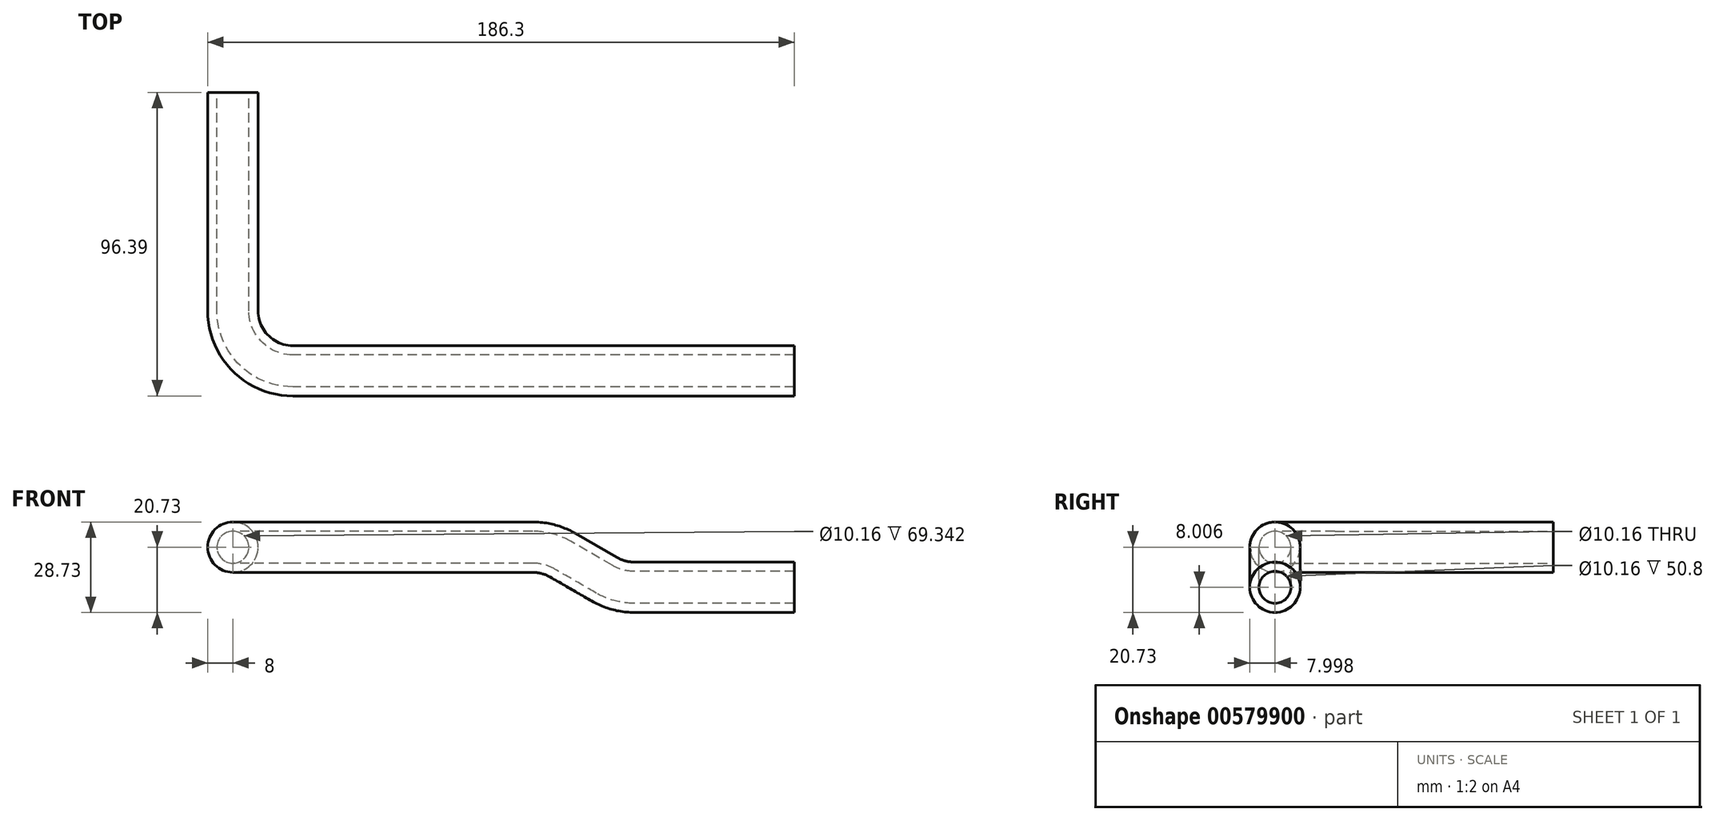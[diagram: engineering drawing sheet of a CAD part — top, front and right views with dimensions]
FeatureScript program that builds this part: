
annotation { "Feature Type Name" : "Feature", "Feature Type Description" : "" }
export const myFeature = defineFeature(function(context is Context, id is Id, definition is map)
    precondition{}
    {
        {
            var Q0;
            Q0=qCreatedBy(makeId("Front.planeOp"),FACE);
            var sketch = newSketch(context, id + "F0", { "sketchPlane" : qUnion([Q0])});
            skCircle(sketch, "E0", {"center": v(0, 0) * mm, "radius": 8 * mm});
            skCircle(sketch, "E1", {"center": v(0, 0) * mm, "radius": 5.08 * mm});
            skSolve(sketch);
        }
        {
            var Q0;
            Q0=qSketchRegion(id+"F0",true);
            extrude(context, id + "F1", {"entities" : qUnion([Q0]), "depth" : 69.34 * mm, "offsetDistance" : 25.4 * mm});
        }
        {
            var Q0;
            Q0=makeQuery(id+"F1.opExtrude","CAP_FACE",FACE,{"disambiguationData":[OSD([sQuery(id+"F0.wireOp",EDGE,"E0"),sQuery(id+"F0.wireOp",EDGE,"E1")])],"isStart":false});
            var sketch = newSketch(context, id + "F2", { "sketchPlane" : qUnion([Q0])});
            skCircle(sketch, "E2", {"center": v(0, 0) * mm, "radius": 5.08 * mm});
            skCircle(sketch, "E3", {"center": v(0, 0) * mm, "radius": 8 * mm});
            skLineSegment(sketch, "E4", {"start": v(19.05, 10.1) * mm, "end": v(19.05, -9.92) * mm});
            skSolve(sketch);
        }
        {
            var Q0;
            Q0 = qSketchRegion(id + "F2", true);
            var Q1;
            Q1=sQuery(id+"F2.wireOp",EDGE,"E4");
            revolve(context, id + "F3", {"operationType" : NewBodyOperationType.ADD, "entities" : qUnion([Q0]), "axis" : qUnion([Q1]), "revolveType" : RevolveType.ONE_DIRECTION, "oppositeDirection" : true, "angle" : 90 * degree});
        }
        {
            var Q0;
            Q0=makeQuery(id+"F3.opRevolve","CAP_FACE",FACE,{"disambiguationData":[OSD([sQuery(id+"F2.wireOp",EDGE,"E2"),sQuery(id+"F2.wireOp",EDGE,"E3")])],"isStart":false});
            var sketch = newSketch(context, id + "F4", { "sketchPlane" : qUnion([Q0])});
            skCircle(sketch, "E5", {"center": v(-88.4, 0) * mm, "radius": 8 * mm});
            skCircle(sketch, "E6", {"center": v(-88.4, 0) * mm, "radius": 5.08 * mm});
            skSolve(sketch);
        }
        {
            var Q0;
            Q0 = qSketchRegion(id + "F4", true);
            extrude(context, id + "F5", {"entities" : qUnion([Q0]), "operationType" : NewBodyOperationType.ADD, "depth" : 76.2 * mm, "offsetDistance" : 25.4 * mm});
        }
        {
            var Q0;
            Q0=makeQuery(id+"F5.opExtrude","CAP_FACE",FACE,{"disambiguationData":[OSD([sQuery(id+"F4.wireOp",EDGE,"E5"),sQuery(id+"F4.wireOp",EDGE,"E6")])],"isStart":false});
            var sketch = newSketch(context, id + "F6", { "sketchPlane" : qUnion([Q0])});
            skCircle(sketch, "E7", {"center": v(-88.4, 0) * mm, "radius": 8 * mm});
            skCircle(sketch, "E8", {"center": v(-88.4, 0) * mm, "radius": 5.08 * mm});
            skLineSegment(sketch, "E9", {"start": v(-98.35, -19.05) * mm, "end": v(-76.26, -19.05) * mm});
            skSolve(sketch);
        }
        {
            var Q0;
            Q0 = qSketchRegion(id + "F6", true);
            var Q1;
            Q1=sQuery(id+"F6.wireOp",EDGE,"E9");
            revolve(context, id + "F7", {"operationType" : NewBodyOperationType.ADD, "entities" : qUnion([Q0]), "axis" : qUnion([Q1]), "revolveType" : RevolveType.ONE_DIRECTION, "angle" : 30 * degree});
        }
        {
            var Q0;
            Q0=makeQuery(id+"F7.opRevolve","CAP_FACE",FACE,{"disambiguationData":[OSD([sQuery(id+"F6.wireOp",EDGE,"E7"),sQuery(id+"F6.wireOp",EDGE,"E8")])],"isStart":false});
            var sketch = newSketch(context, id + "F8", { "sketchPlane" : qUnion([Q0])});
            skCircle(sketch, "E10", {"center": v(-88.4, 50.18) * mm, "radius": 8 * mm});
            skCircle(sketch, "E11", {"center": v(-88.4, 50.18) * mm, "radius": 5.08 * mm});
            skSolve(sketch);
        }
        {
            var Q0;
            Q0 = qSketchRegion(id + "F8", true);
            extrude(context, id + "F9", {"entities" : qUnion([Q0]), "operationType" : NewBodyOperationType.ADD, "depth" : 15.24 * mm, "offsetDistance" : 25.4 * mm});
        }
        {
            var Q0;
            Q0=makeQuery(id+"F9.opExtrude","CAP_FACE",FACE,{"disambiguationData":[OSD([sQuery(id+"F8.wireOp",EDGE,"E10"),sQuery(id+"F8.wireOp",EDGE,"E11")])],"isStart":false});
            var sketch = newSketch(context, id + "F10", { "sketchPlane" : qUnion([Q0])});
            skCircle(sketch, "E12", {"center": v(-88.4, 50.18) * mm, "radius": 8 * mm});
            skCircle(sketch, "E13", {"center": v(-88.4, 50.18) * mm, "radius": 5.08 * mm});
            skLineSegment(sketch, "E14", {"start": v(-99.85, 69.23) * mm, "end": v(-76.66, 69.23) * mm});
            skSolve(sketch);
        }
        {
            var Q0;
            Q0 = qSketchRegion(id + "F10", true);
            var Q1;
            Q1=sQuery(id+"F10.wireOp",EDGE,"E14");
            revolve(context, id + "F11", {"operationType" : NewBodyOperationType.ADD, "entities" : qUnion([Q0]), "axis" : qUnion([Q1]), "revolveType" : RevolveType.ONE_DIRECTION, "oppositeDirection" : true, "angle" : 30 * degree});
        }
        {
            var Q0;
            Q0=makeQuery(id+"F11.opRevolve","CAP_FACE",FACE,{"disambiguationData":[OSD([sQuery(id+"F10.wireOp",EDGE,"E12"),sQuery(id+"F10.wireOp",EDGE,"E13")])],"isStart":false});
            var sketch = newSketch(context, id + "F12", { "sketchPlane" : qUnion([Q0])});
            skCircle(sketch, "E15", {"center": v(-88.4, -12.72) * mm, "radius": 8 * mm});
            skCircle(sketch, "E16", {"center": v(-88.4, -12.72) * mm, "radius": 5.08 * mm});
            skSolve(sketch);
        }
        {
            var Q0;
            Q0 = qSketchRegion(id + "F12", true);
            extrude(context, id + "F13", {"entities" : qUnion([Q0]), "operationType" : NewBodyOperationType.ADD, "depth" : 50.8 * mm, "offsetDistance" : 25.4 * mm});
        }
    });
